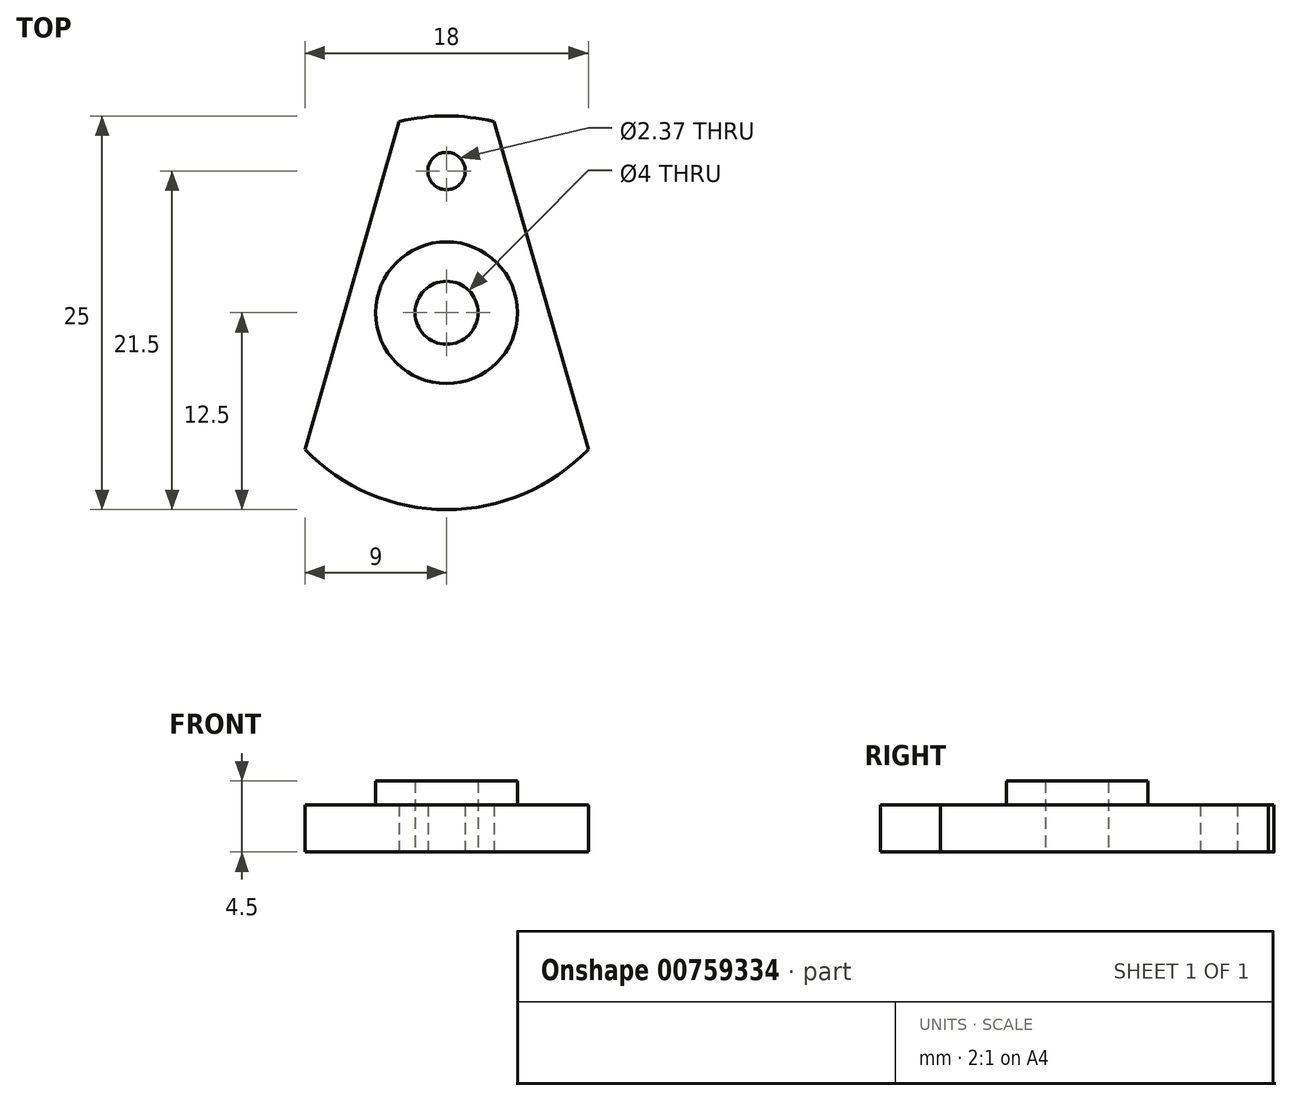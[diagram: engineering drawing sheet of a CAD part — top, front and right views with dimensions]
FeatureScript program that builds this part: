
annotation { "Feature Type Name" : "Feature", "Feature Type Description" : "" }
export const myFeature = defineFeature(function(context is Context, id is Id, definition is map)
    precondition{}
    {
        {
            var Q0;
            Q0=qCreatedBy(makeId("Top.planeOp"),FACE);
            var sketch = newSketch(context, id + "F0", { "sketchPlane" : qUnion([Q0])});
            skArc(sketch, "E0", {"start": v(3, 12.13) * mm, "mid": v(0, 12.5) * mm, "end": v(-3, 12.13) * mm});
            skLineSegment(sketch, "E1", {"start": v(9, -8.67) * mm, "end": v(3, 12.13) * mm});
            skLineSegment(sketch, "E2", {"start": v(-9, -8.67) * mm, "end": v(-3, 12.13) * mm});
            skArc(sketch, "E3.trimOffspring", {"start": v(-9, -8.67) * mm, "mid": v(0, -12.5) * mm, "end": v(9, -8.67) * mm});
            skCircle(sketch, "E4", {"center": v(0, 9) * mm, "radius": 1.19 * mm});
            skCircle(sketch, "E5", {"center": v(0, 0) * mm, "radius": 4.5 * mm});
            skCircle(sketch, "E6", {"center": v(0, 0) * mm, "radius": 2 * mm});
            skSolve(sketch);
        }
        {
            var Q0;
            Q0=makeQuery(id+"F0.imprint","IMPRINT",FACE,{"disambiguationData":[TD([[makeQuery(id+"F0.imprint","IMPRINT",EDGE,{"derivedFrom":sQuery(id+"F0.wireOp",EDGE,"E0")}),1.0]])]});
            extrude(context, id + "F1", {"entities" : qUnion([Q0]), "depth" : 3 * mm, "offsetDistance" : 25 * mm});
        }
        {
            var Q0;
            Q0=makeQuery(id+"F0.imprint","IMPRINT",FACE,{"disambiguationData":[TD([[makeQuery(id+"F0.imprint","IMPRINT",EDGE,{"derivedFrom":sQuery(id+"F0.wireOp",EDGE,"E5")}),1.0]])]});
            extrude(context, id + "F2", {"entities" : qUnion([Q0]), "operationType" : NewBodyOperationType.ADD, "depth" : 4.5 * mm, "offsetDistance" : 25 * mm});
        }
    });
